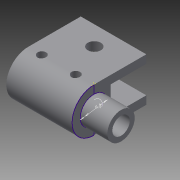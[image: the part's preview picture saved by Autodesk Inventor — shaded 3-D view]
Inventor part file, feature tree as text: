
AUTODESK INVENTOR PART (.ipt)
format: ipt  version: 2015 (Build 190159000, 159)  size: 158,208 bytes
history: native  units: in
note: dims shown in document units (in); Inventor stores cm internally (conversion verified against a paired STEP export)
features: extrude x6, sketch x2
ambient origin geometry x8: Origin, YZ Plane, XZ Plane, XY Plane, X Axis, Y Axis, Z Axis, Center Point
bodies: Solid1 (feature_tree)
feature tree (8):
  sketch  "Sketch1"  dims[d0=11.0236in d1=0.6693in]
  extrude  "Extrusion1"  Depth=0.6693in
  extrude  "Extrusion2"  Depth=0.3937in
  sketch  "Sketch2"  dims[d2=11.0236in d3=0.3937in d4=1.5748in d5=4.9213in d6=2.7559in d7=0.7874in d8=0.7874in d11=0.126in d12=0.4724in d16=0.1181in d18=0.189in d19=0.6299in d20=0.0in d21=0.3937in d22=0.0in d23=0.252in d24=0.9449in d25=0.0in d26=0.9449in d27=0.0in d28=0.2756in d29=0.2756in d30=0.122in d31=0.122in d32=0.7874in d33=0.0in d34=0.3937in d35=0.3937in d36=0.0in]
  extrude  "Extrusion3"  Depth=0.3937in
  extrude  "Extrusion4"  Depth=0.3937in
  extrude  "Extrusion5"  Depth=2.7559in
  extrude  "Extrusion6"  Depth=0.3937in
